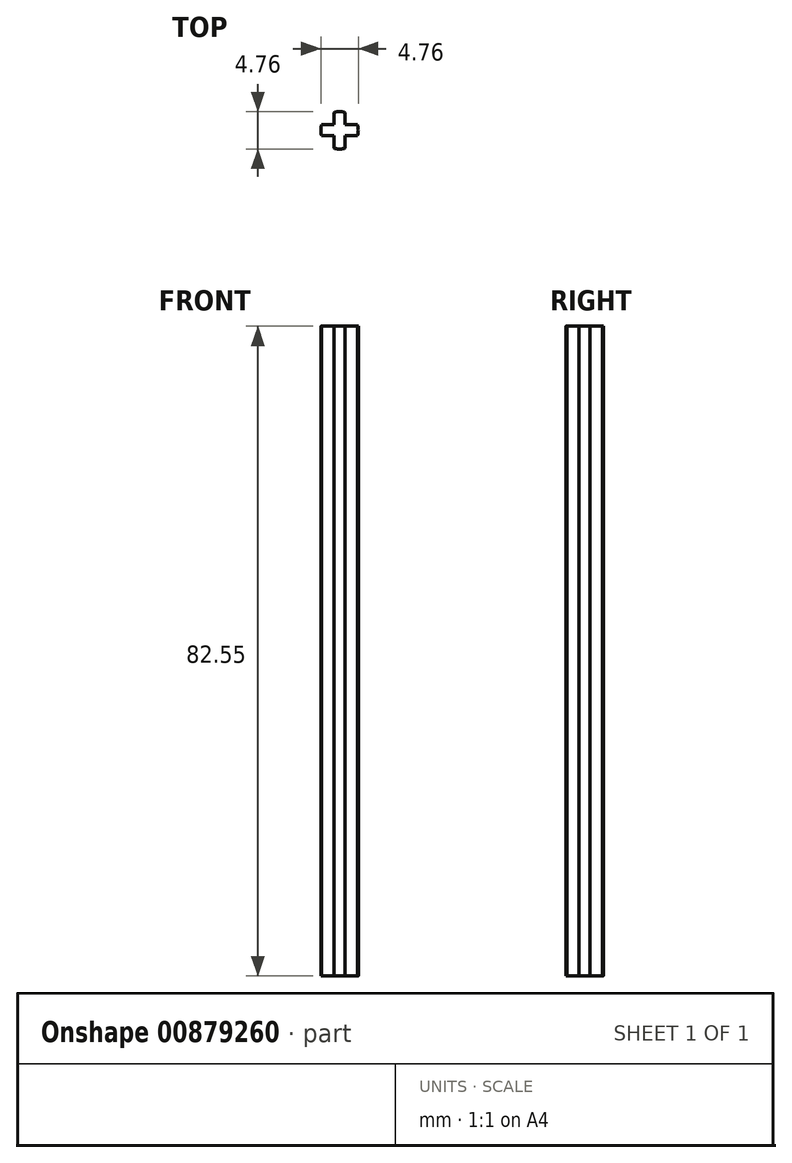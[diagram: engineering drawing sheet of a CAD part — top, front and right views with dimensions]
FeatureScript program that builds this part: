
annotation { "Feature Type Name" : "Feature", "Feature Type Description" : "" }
export const myFeature = defineFeature(function(context is Context, id is Id, definition is map)
    precondition{}
    {
        {
            var Q0;
            Q0=qCreatedBy(makeId("Top.planeOp"),FACE);
            var sketch = newSketch(context, id + "F0", { "sketchPlane" : qUnion([Q0])});
            skArc(sketch, "E0", {"start": v(-11.58, 9.38) * mm, "mid": v(-10.88, 9.28) * mm, "end": v(-10.18, 9.38) * mm});
            skLineSegment(sketch, "E1.bottom", {"start": v(-11.58, 10.96) * mm, "end": v(-13.16, 10.96) * mm});
            skLineSegment(sketch, "E1.left", {"start": v(-11.58, 10.96) * mm, "end": v(-11.58, 9.38) * mm});
            skLineSegment(sketch, "E2.bottom", {"start": v(-10.18, 10.96) * mm, "end": v(-8.6, 10.96) * mm});
            skLineSegment(sketch, "E2.left", {"start": v(-10.18, 10.96) * mm, "end": v(-10.18, 9.38) * mm});
            skLineSegment(sketch, "E3.bottom", {"start": v(-10.18, 12.36) * mm, "end": v(-8.6, 12.36) * mm});
            skLineSegment(sketch, "E3.left", {"start": v(-10.18, 12.36) * mm, "end": v(-10.18, 13.94) * mm});
            skLineSegment(sketch, "E4.bottom", {"start": v(-11.58, 12.36) * mm, "end": v(-13.16, 12.36) * mm});
            skLineSegment(sketch, "E4.left", {"start": v(-11.58, 12.36) * mm, "end": v(-11.58, 13.94) * mm});
            skPoint(sketch, "E5.orphan", {"position": v(-10.88, 9.28) * mm});
            skPoint(sketch, "E4.top.end.orphan", {"position": v(-13.84, 14.05) * mm});
            skArc(sketch, "E6.trimOffspring", {"start": v(-13.16, 12.36) * mm, "mid": v(-13.26, 11.66) * mm, "end": v(-13.16, 10.96) * mm});
            skArc(sketch, "E7.trimOffspring", {"start": v(-10.18, 13.94) * mm, "mid": v(-10.88, 14.04) * mm, "end": v(-11.58, 13.94) * mm});
            skPoint(sketch, "E3.right.end.orphan", {"position": v(-8.3, 14.05) * mm});
            skArc(sketch, "E8.trimOffspring", {"start": v(-8.6, 10.96) * mm, "mid": v(-8.5, 11.66) * mm, "end": v(-8.6, 12.36) * mm});
            skSolve(sketch);
        }
        {
            var Q0;
            Q0=makeQuery(id+"F0.imprint","IMPRINT",FACE,{"disambiguationData":[TD([[makeQuery(id+"F0.imprint","IMPRINT",EDGE,{"derivedFrom":sQuery(id+"F0.wireOp",EDGE,"E0")}),1.0]])]});
            extrude(context, id + "F1", {"entities" : qUnion([Q0]), "depth" : 82.55 * mm, "offsetDistance" : 25.4 * mm});
        }
    });
